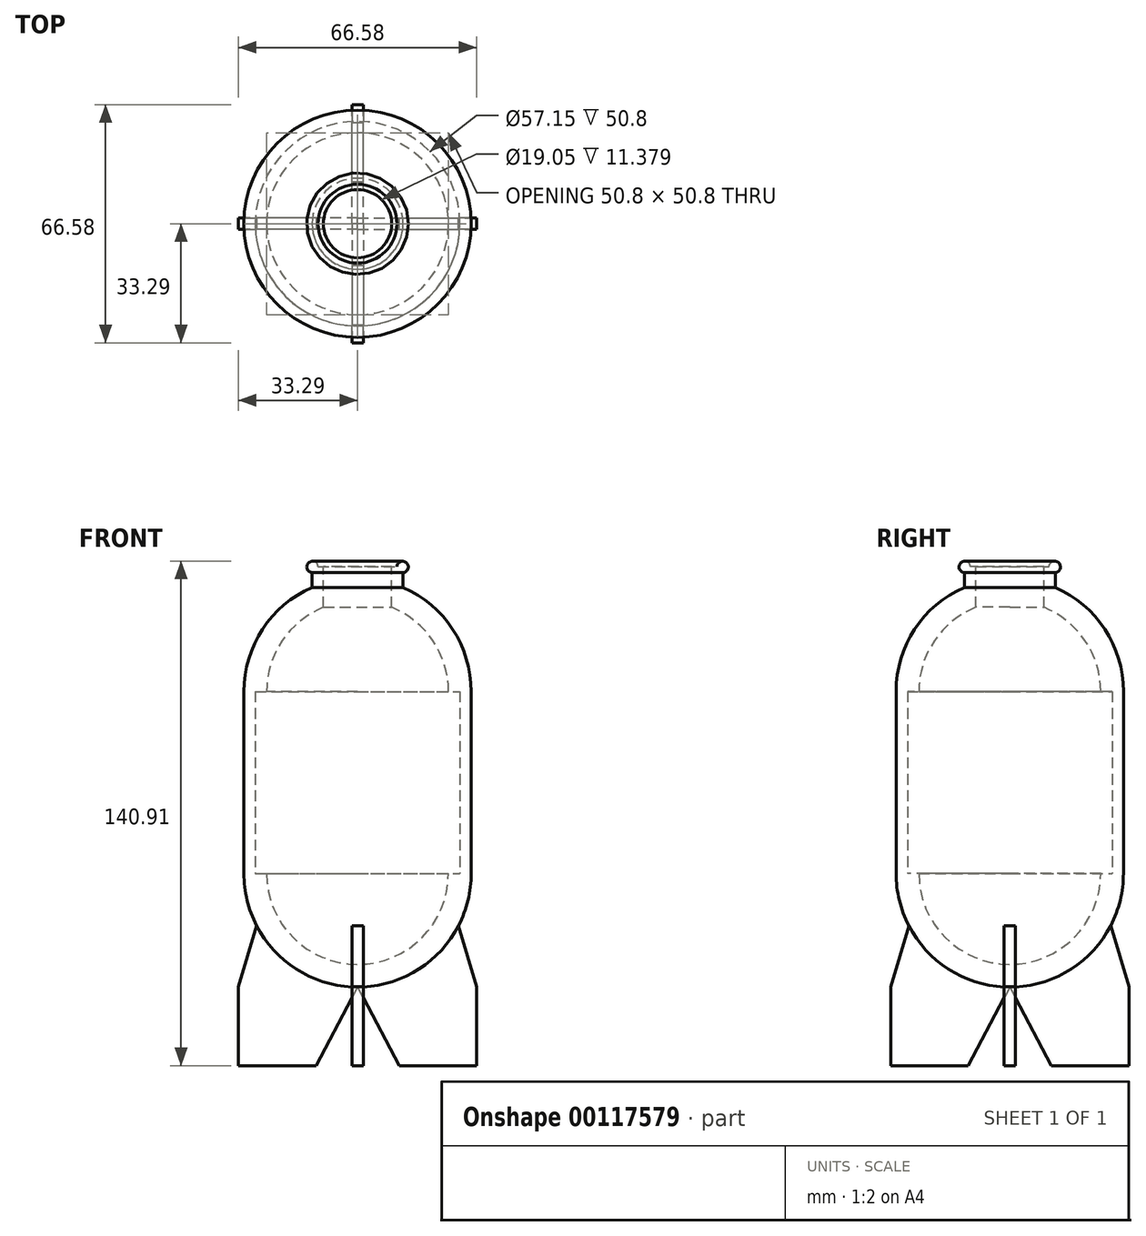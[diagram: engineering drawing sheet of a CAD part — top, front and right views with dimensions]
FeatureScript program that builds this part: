
annotation { "Feature Type Name" : "Feature", "Feature Type Description" : "" }
export const myFeature = defineFeature(function(context is Context, id is Id, definition is map)
    precondition{}
    {
        {
            var Q0;
            Q0=qCreatedBy(makeId("Top.planeOp"),FACE);
            var sketch = newSketch(context, id + "F0", { "sketchPlane" : qUnion([Q0])});
            skCircle(sketch, "E0", {"center": v(0, 0) * mm, "radius": 31.75 * mm});
            skCircle(sketch, "E1", {"center": v(0, 0) * mm, "radius": 28.58 * mm});
            skSolve(sketch);
        }
        {
            var Q0;
            Q0 = qSketchRegion(id + "F0", true);
            extrude(context, id + "F1", {"entities" : qUnion([Q0]), "endBound" : BoundingType.SYMMETRIC, "depth" : 50.8 * mm});
        }
        {
            var Q0;
            Q0=makeQuery(id+"F1.opExtrude","CAP_FACE",FACE,{"disambiguationData":[OSD([sQuery(id+"F0.wireOp",EDGE,"E0"),sQuery(id+"F0.wireOp",EDGE,"E1")])],"isStart":false});
            var sketch = newSketch(context, id + "F2", { "sketchPlane" : qUnion([Q0])});
            skArc(sketch, "E2", {"start": v(0, -31.75) * mm, "mid": v(31.75, 0) * mm, "end": v(0, 31.75) * mm});
            skArc(sketch, "E3", {"start": v(0, -25.4) * mm, "mid": v(25.4, 0) * mm, "end": v(0, 25.4) * mm});
            skLineSegment(sketch, "E4", {"start": v(0, 31.75) * mm, "end": v(0, -31.75) * mm, "construction": true});
            skLineSegment(sketch, "E5", {"start": v(0, 31.75) * mm, "end": v(0, 25.4) * mm});
            skLineSegment(sketch, "E6", {"start": v(0, -31.75) * mm, "end": v(0, -25.4) * mm});
            skSolve(sketch);
        }
        {
            var Q0;
            Q0 = qSketchRegion(id + "F2", true);
            var Q1;
            Q1=sQuery(id+"F2.wireOp",EDGE,"E4");
            revolve(context, id + "F3", {"operationType" : NewBodyOperationType.ADD, "entities" : qUnion([Q0]), "axis" : qUnion([Q1]), "revolveType" : RevolveType.ONE_DIRECTION, "angle" : 180 * degree});
        }
        {
            var Q0;
            Q0=makeQuery(id+"F1.opExtrude","SWEPT_BODY",BODY,{"disambiguationData":[OSD([sQuery(id+"F0.wireOp",EDGE,"E0"),sQuery(id+"F0.wireOp",EDGE,"E1")])]});
            var Q1;
            Q1=qCreatedBy(makeId("Top.planeOp"),FACE);
            mirror(context, id + "F4", {"operationType" : NewBodyOperationType.ADD, "entities" : qUnion([Q0]), "mirrorPlane" : qUnion([Q1])});
        }
        {
            var Q0;
            Q0=qCreatedBy(makeId("Top.planeOp"),FACE);
            cPlane(context, id + "F5", {"entities" : qUnion([Q0]), "cplaneType" : CPlaneType.OFFSET, "offset" : 57.15 * mm, "width" : 152.4 * mm, "height" : 152.4 * mm});
        }
        {
            var Q0;
            Q0=qCreatedBy(id+"F5.planeOp",FACE);
            var sketch = newSketch(context, id + "F6", { "sketchPlane" : qUnion([Q0])});
            skCircle(sketch, "E7", {"center": v(0, 0) * mm, "radius": 12.7 * mm});
            skSolve(sketch);
        }
        {
            var Q0;
            Q0 = qSketchRegion(id + "F6", true);
            extrude(context, id + "F7", {"entities" : qUnion([Q0]), "operationType" : NewBodyOperationType.ADD, "endBound" : BoundingType.SYMMETRIC, "depth" : 6.35 * mm});
        }
        {
            var Q0;
            Q0=makeQuery(id+"F7.opExtrude","CAP_FACE",FACE,{"disambiguationData":[OSD([sQuery(id+"F6.wireOp",EDGE,"E7")])],"isStart":false});
            var sketch = newSketch(context, id + "F8", { "sketchPlane" : qUnion([Q0])});
            skCircle(sketch, "E8", {"center": v(0, 0) * mm, "radius": 9.53 * mm});
            skSolve(sketch);
        }
        {
            var Q0;
            Q0 = qSketchRegion(id + "F8", true);
            extrude(context, id + "F9", {"entities" : qUnion([Q0]), "operationType" : NewBodyOperationType.REMOVE, "oppositeDirection" : true, "depth" : 25.4 * mm});
        }
        {
            var Q0;
            Q0=qCreatedBy(makeId("Front.planeOp"),FACE);
            var sketch = newSketch(context, id + "F10", { "sketchPlane" : qUnion([Q0])});
            skArc(sketch, "E9", {"start": v(0, -57.15) * mm, "mid": v(16.5, -52.53) * mm, "end": v(28.2, -40) * mm});
            skLineSegment(sketch, "E10", {"start": v(0, -57.15) * mm, "end": v(11.6, -79.09) * mm});
            skLineSegment(sketch, "E11", {"start": v(11.6, -79.09) * mm, "end": v(33.29, -79.09) * mm});
            skLineSegment(sketch, "E12", {"start": v(33.29, -79.09) * mm, "end": v(33.29, -57.05) * mm});
            skLineSegment(sketch, "E13", {"start": v(33.29, -57.05) * mm, "end": v(28.2, -40) * mm});
            skPoint(sketch, "E14.orphan", {"position": v(31.75, -25.4) * mm});
            skPoint(sketch, "E15.orphan", {"position": v(-31.75, -25.4) * mm});
            skSolve(sketch);
        }
        {
            var Q0;
            Q0 = qSketchRegion(id + "F10", true);
            extrude(context, id + "F11", {"entities" : qUnion([Q0]), "operationType" : NewBodyOperationType.ADD, "endBound" : BoundingType.SYMMETRIC, "depth" : 3.17 * mm});
        }
        {
            var Q0;
            Q0=qCreatedBy(makeId("Right.planeOp"),FACE);
            var sketch = newSketch(context, id + "F12", { "sketchPlane" : qUnion([Q0])});
            skLineSegment(sketch, "E16", {"start": v(0, 60.8) * mm, "end": v(0, -57.24) * mm, "construction": true});
            skSolve(sketch);
        }
        {
            var Q0;
            Q0=makeQuery(id+"F11.opExtrude","SWEPT_BODY",BODY,{"disambiguationData":[OSD([sQuery(id+"F10.wireOp",EDGE,"E9"),sQuery(id+"F10.wireOp",EDGE,"E10"),sQuery(id+"F10.wireOp",EDGE,"E11"),sQuery(id+"F10.wireOp",EDGE,"E12"),sQuery(id+"F10.wireOp",EDGE,"E13")])]});
            var Q1;
            Q1=sQuery(id+"F12.wireOp",EDGE,"E16");
            circularPattern(context, id + "F13", {"entities" : qUnion([Q0]), "axis" : qUnion([Q1]), "angle" : 90 * degree, "instanceCount" : 4});
        }
        {
            var Q0;
            Q0=qCreatedBy(makeId("Front.planeOp"),FACE);
            var sketch = newSketch(context, id + "F14", { "sketchPlane" : qUnion([Q0])});
            skLineSegment(sketch, "E17", {"start": v(0, 46.85) * mm, "end": v(0, 31.4) * mm, "construction": true});
            skCircle(sketch, "E18", {"center": v(12.6, 60.23) * mm, "radius": 1.59 * mm});
            skSolve(sketch);
        }
        {
            var Q0;
            Q0 = qSketchRegion(id + "F14", true);
            var Q1;
            Q1=sQuery(id+"F14.wireOp",EDGE,"E17");
            revolve(context, id + "F15", {"operationType" : NewBodyOperationType.ADD, "entities" : qUnion([Q0]), "axis" : qUnion([Q1]), "revolveType" : RevolveType.FULL});
        }
    });
